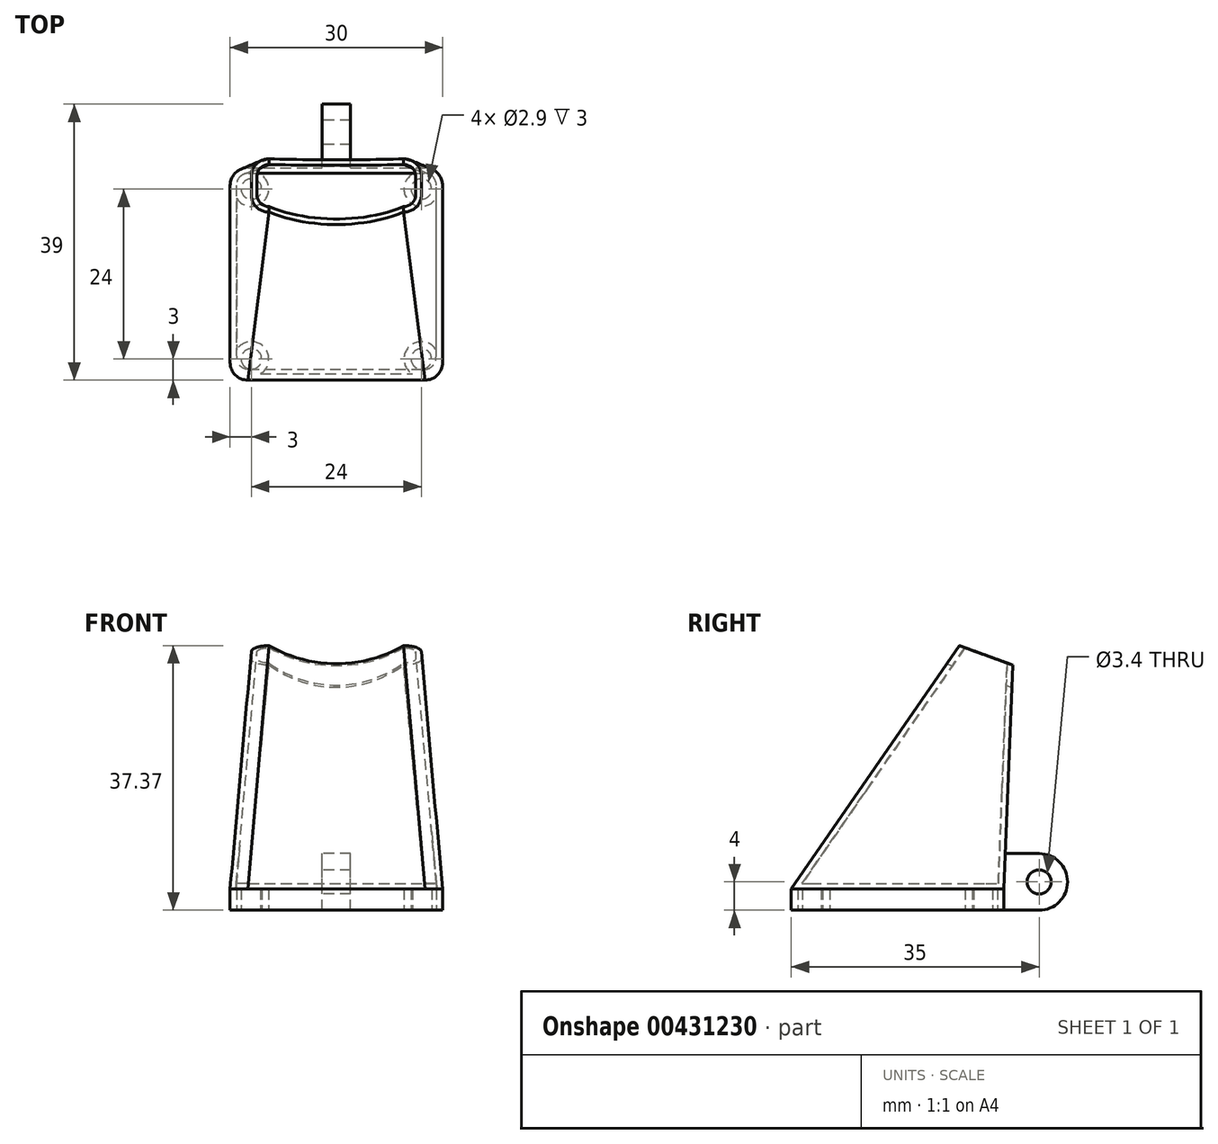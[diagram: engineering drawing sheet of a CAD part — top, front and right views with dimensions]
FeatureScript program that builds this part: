
annotation { "Feature Type Name" : "Feature", "Feature Type Description" : "" }
export const myFeature = defineFeature(function(context is Context, id is Id, definition is map)
    precondition{}
    {
        {
            var Q0;
            Q0=qCreatedBy(makeId("Top.planeOp"),FACE);
            var sketch = newSketch(context, id + "F0", { "sketchPlane" : qUnion([Q0])});
            skLineSegment(sketch, "E0", {"start": v(-15, 0) * mm, "end": v(-15, 12.5) * mm});
            skLineSegment(sketch, "E1", {"start": v(-12.5, 15) * mm, "end": v(0, 15) * mm});
            skPoint(sketch, "E2.visualSharp", {"position": v(-15, 15) * mm});
            skArc(sketch, "E2.filletArc", {"start": v(-12.5, 15) * mm, "mid": v(-14.27, 14.27) * mm, "end": v(-15, 12.5) * mm});
            skCircle(sketch, "E3", {"center": v(-12, 12) * mm, "radius": 1.45 * mm});
            skLineSegment(sketch, "E4", {"start": v(0, 14.1) * mm, "end": v(-10.74, 14.1) * mm});
            skLineSegment(sketch, "E5", {"start": v(-14.1, 0) * mm, "end": v(-14.1, 10.74) * mm});
            skArc(sketch, "E6", {"start": v(-10.74, 14.1) * mm, "mid": v(-10.27, 10.27) * mm, "end": v(-14.1, 10.74) * mm});
            skLineSegment(sketch, "E7.MirrorCS", {"start": v(12.5, 15) * mm, "end": v(0, 15) * mm});
            skArc(sketch, "E8.MirrorCS", {"start": v(12.5, 15) * mm, "mid": v(14.27, 14.27) * mm, "end": v(15, 12.5) * mm});
            skCircle(sketch, "E9.MirrorC", {"center": v(12, 12) * mm, "radius": 1.45 * mm});
            skPoint(sketch, "E10.MirrorP", {"position": v(15, 15) * mm});
            skLineSegment(sketch, "E11.MirrorCS", {"start": v(15, 0) * mm, "end": v(15, 12.5) * mm});
            skArc(sketch, "E12.MirrorCS", {"start": v(10.74, 14.1) * mm, "mid": v(10.27, 10.27) * mm, "end": v(14.1, 10.74) * mm});
            skLineSegment(sketch, "E13.MirrorCS", {"start": v(14.1, 0) * mm, "end": v(14.1, 10.74) * mm});
            skLineSegment(sketch, "E14.MirrorCS", {"start": v(0, 14.1) * mm, "end": v(10.74, 14.1) * mm});
            skLineSegment(sketch, "E15.MirrorCS", {"start": v(-14.1, 0) * mm, "end": v(-14.1, -10.74) * mm});
            skArc(sketch, "E16.MirrorCS", {"start": v(12.5, -15) * mm, "mid": v(14.27, -14.27) * mm, "end": v(15, -12.5) * mm});
            skLineSegment(sketch, "E17.MirrorCS", {"start": v(12.5, -15) * mm, "end": v(0, -15) * mm});
            skCircle(sketch, "E18.MirrorC", {"center": v(12, -12) * mm, "radius": 1.45 * mm});
            skLineSegment(sketch, "E19.MirrorCS", {"start": v(15, 0) * mm, "end": v(15, -12.5) * mm});
            skArc(sketch, "E20.MirrorCS", {"start": v(10.74, -14.1) * mm, "mid": v(10.27, -10.27) * mm, "end": v(14.1, -10.74) * mm});
            skLineSegment(sketch, "E21.MirrorCS", {"start": v(14.1, 0) * mm, "end": v(14.1, -10.74) * mm});
            skLineSegment(sketch, "E22.MirrorCS", {"start": v(-15, 0) * mm, "end": v(-15, -12.5) * mm});
            skLineSegment(sketch, "E23.MirrorCS", {"start": v(0, -14.1) * mm, "end": v(10.74, -14.1) * mm});
            skPoint(sketch, "E24.MirrorP", {"position": v(15, -15) * mm});
            skLineSegment(sketch, "E25.MirrorCS", {"start": v(0, -14.1) * mm, "end": v(-10.74, -14.1) * mm});
            skArc(sketch, "E26.MirrorCS", {"start": v(-10.74, -14.1) * mm, "mid": v(-10.27, -10.27) * mm, "end": v(-14.1, -10.74) * mm});
            skArc(sketch, "E27.MirrorCS", {"start": v(-12.5, -15) * mm, "mid": v(-14.27, -14.27) * mm, "end": v(-15, -12.5) * mm});
            skLineSegment(sketch, "E28.MirrorCS", {"start": v(-12.5, -15) * mm, "end": v(0, -15) * mm});
            skCircle(sketch, "E29.MirrorC", {"center": v(-12, -12) * mm, "radius": 1.45 * mm});
            skPoint(sketch, "E30.MirrorP", {"position": v(-15, -15) * mm});
            skSolve(sketch);
        }
        {
            var Q0;
            Q0 = qSketchRegion(id + "F0", true);
            extrude(context, id + "F1", {"entities" : qUnion([Q0]), "depth" : 3 * mm});
        }
        {
            var Q0;
            Q0=qCreatedBy(makeId("Right.planeOp"),FACE);
            var sketch = newSketch(context, id + "F2", { "sketchPlane" : qUnion([Q0])});
            skLineSegment(sketch, "E31.0", {"start": v(12.5, 3) * mm, "end": v(-12.5, 3) * mm, "construction": true});
            skLineSegment(sketch, "E32", {"start": v(0, 3) * mm, "end": v(0, 36) * mm, "construction": true});
            skPoint(sketch, "E32.endSnap0", {"position": v(0, 3) * mm});
            skLineSegment(sketch, "E33", {"start": v(12.5, 3) * mm, "end": v(12.5, 36) * mm, "construction": true});
            skLineSegment(sketch, "E34", {"start": v(6.18, 38.3) * mm, "end": v(18.52, 33.8) * mm, "construction": true});
            skSolve(sketch);
        }
        {
            var Q0;
            Q0=sQuery(id+"F2.wireOp",EDGE,"E34");
            cPlane(context, id + "F3", {"entities" : qUnion([Q0]), "cplaneType" : CPlaneType.LINE_ANGLE, "offset" : 25 * mm, "angle" : 0 * degree, "width" : 150 * mm, "height" : 150 * mm});
        }
        {
            var Q0;
            Q0=qCreatedBy(id+"F3.planeOp",FACE);
            var sketch = newSketch(context, id + "F4", { "sketchPlane" : qUnion([Q0])});
            skLineSegment(sketch, "E35", {"start": v(0, -0.57) * mm, "end": v(-15.7, -0.57) * mm});
            skLineSegment(sketch, "E36.0", {"start": v(-15, -12.77) * mm, "end": v(-15, 10.72) * mm, "construction": true});
            skLineSegment(sketch, "E37.0", {"start": v(15, 10.72) * mm, "end": v(15, -12.77) * mm, "construction": true});
            skLineSegment(sketch, "E38.bottom", {"start": v(-9.5, -4.57) * mm, "end": v(9.5, -4.57) * mm});
            skLineSegment(sketch, "E38.top", {"start": v(-9.5, 3.43) * mm, "end": v(9.5, 3.43) * mm});
            skLineSegment(sketch, "E38.left", {"start": v(-12, -2.07) * mm, "end": v(-12, 0.93) * mm});
            skLineSegment(sketch, "E38.right", {"start": v(12, -2.07) * mm, "end": v(12, 0.93) * mm});
            skPoint(sketch, "E39.visualSharp", {"position": v(-12, 3.43) * mm});
            skArc(sketch, "E39.filletArc", {"start": v(-9.5, 3.43) * mm, "mid": v(-11.27, 2.7) * mm, "end": v(-12, 0.93) * mm});
            skPoint(sketch, "E40.visualSharp", {"position": v(-12, -4.57) * mm});
            skArc(sketch, "E40.filletArc", {"start": v(-12, -2.07) * mm, "mid": v(-11.27, -3.83) * mm, "end": v(-9.5, -4.57) * mm});
            skPoint(sketch, "E41.visualSharp", {"position": v(12, -4.57) * mm});
            skArc(sketch, "E41.filletArc", {"start": v(9.5, -4.57) * mm, "mid": v(11.27, -3.83) * mm, "end": v(12, -2.07) * mm});
            skPoint(sketch, "E42.visualSharp", {"position": v(12, 3.43) * mm});
            skArc(sketch, "E42.filletArc", {"start": v(12, 0.93) * mm, "mid": v(11.27, 2.7) * mm, "end": v(9.5, 3.43) * mm});
            skSolve(sketch);
        }
        {
            var Q0;
            Q0=makeQuery(id+"F1.opExtrude","CAP_FACE",FACE,{"disambiguationData":[OSD([sQuery(id+"F0.wireOp",EDGE,"E0"),sQuery(id+"F0.wireOp",EDGE,"E1"),sQuery(id+"F0.wireOp",EDGE,"E2.filletArc"),sQuery(id+"F0.wireOp",EDGE,"E3"),sQuery(id+"F0.wireOp",EDGE,"E4"),sQuery(id+"F0.wireOp",EDGE,"E5"),sQuery(id+"F0.wireOp",EDGE,"E6"),sQuery(id+"F0.wireOp",EDGE,"E7.MirrorCS"),sQuery(id+"F0.wireOp",EDGE,"E8.MirrorCS"),sQuery(id+"F0.wireOp",EDGE,"E9.MirrorC"),sQuery(id+"F0.wireOp",EDGE,"E11.MirrorCS"),sQuery(id+"F0.wireOp",EDGE,"E12.MirrorCS"),sQuery(id+"F0.wireOp",EDGE,"E13.MirrorCS"),sQuery(id+"F0.wireOp",EDGE,"E14.MirrorCS"),sQuery(id+"F0.wireOp",EDGE,"E15.MirrorCS"),sQuery(id+"F0.wireOp",EDGE,"E16.MirrorCS"),sQuery(id+"F0.wireOp",EDGE,"E17.MirrorCS"),sQuery(id+"F0.wireOp",EDGE,"E18.MirrorC"),sQuery(id+"F0.wireOp",EDGE,"E19.MirrorCS"),sQuery(id+"F0.wireOp",EDGE,"E20.MirrorCS"),sQuery(id+"F0.wireOp",EDGE,"E21.MirrorCS"),sQuery(id+"F0.wireOp",EDGE,"E22.MirrorCS"),sQuery(id+"F0.wireOp",EDGE,"E23.MirrorCS"),sQuery(id+"F0.wireOp",EDGE,"E25.MirrorCS"),sQuery(id+"F0.wireOp",EDGE,"E26.MirrorCS"),sQuery(id+"F0.wireOp",EDGE,"E27.MirrorCS"),sQuery(id+"F0.wireOp",EDGE,"E28.MirrorCS"),sQuery(id+"F0.wireOp",EDGE,"E29.MirrorC")])],"isStart":false});
            var sketch = newSketch(context, id + "F5", { "sketchPlane" : qUnion([Q0])});
            skArc(sketch, "E43.0", {"start": v(-12.5, -15) * mm, "mid": v(-14.27, -14.27) * mm, "end": v(-15, -12.5) * mm});
            skLineSegment(sketch, "E44.0", {"start": v(-15, -12.5) * mm, "end": v(-15, 12.5) * mm});
            skArc(sketch, "E45.0", {"start": v(-12.5, 15) * mm, "mid": v(-14.27, 14.27) * mm, "end": v(-15, 12.5) * mm});
            skLineSegment(sketch, "E46.0", {"start": v(12.5, 15) * mm, "end": v(-12.5, 15) * mm});
            skArc(sketch, "E47.0", {"start": v(12.5, 15) * mm, "mid": v(14.27, 14.27) * mm, "end": v(15, 12.5) * mm});
            skLineSegment(sketch, "E48.0", {"start": v(15, 12.5) * mm, "end": v(15, -12.5) * mm});
            skArc(sketch, "E49.0", {"start": v(12.5, -15) * mm, "mid": v(14.27, -14.27) * mm, "end": v(15, -12.5) * mm});
            skLineSegment(sketch, "E50.0", {"start": v(12.5, -15) * mm, "end": v(-12.5, -15) * mm});
            skSolve(sketch);
        }
        {
            var Q1;
            Q1 = qSketchRegion(id + "F5", true);
            var Q2;
            Q2=makeQuery(id+"F4.imprint","IMPRINT",FACE,{"disambiguationData":[TD([[makeQuery(id+"F4.imprint","IMPRINT",EDGE,{"derivedFrom":sQuery(id+"F4.wireOp",EDGE,"E38.bottom")}),1.0]])]});
            loft(context, id + "F6", {"sheetProfilesArray" : [{ "sheetProfileEntities" : qUnion([Q1]) }, { "sheetProfileEntities" : qUnion([Q2]) }]});
        }
        {
            var Q0;
            Q0=makeQuery(id+"F6.opLoft","CAP_FACE",FACE,{"disambiguationData":[OSD([makeQuery(id+"F5.imprint","IMPRINT",FACE,{"disambiguationData":[TD([[makeQuery(id+"F5.imprint","IMPRINT",EDGE,{"derivedFrom":sQuery(id+"F5.wireOp",EDGE,"E43.0")}),-1.0]])]})])],"isStart":true});
            var Q1;
            Q1=makeQuery(id+"F6.opLoft","CAP_FACE",FACE,{"disambiguationData":[OSD([makeQuery(id+"F4.imprint","IMPRINT",FACE,{"disambiguationData":[TD([[makeQuery(id+"F4.imprint","IMPRINT",EDGE,{"derivedFrom":sQuery(id+"F4.wireOp",EDGE,"E38.bottom")}),1.0]])]})])],"isStart":true});
            shell(context, id + "F7", {"entities" : qUnion([Q0, Q1]), "thickness" : 0.8 * mm});
        }
        {
            var Q0;
            Q0=makeQuery(id+"F6.opLoft","SWEPT_BODY",BODY,{"disambiguationData":[OSD([makeQuery(id+"F4.imprint","IMPRINT",FACE,{"disambiguationData":[TD([[makeQuery(id+"F4.imprint","IMPRINT",EDGE,{"derivedFrom":sQuery(id+"F4.wireOp",EDGE,"E38.bottom")}),1.0]])]}),makeQuery(id+"F5.imprint","IMPRINT",FACE,{"disambiguationData":[TD([[makeQuery(id+"F5.imprint","IMPRINT",EDGE,{"derivedFrom":makeQuery(id+"F1.opExtrude","CAP_EDGE",EDGE,{"disambiguationData":[OSD([sQuery(id+"F0.wireOp",EDGE,"E3")])],"isStart":false})}),1.0]])]})])]});
            var Q1;
            Q1=makeQuery(id+"F1.opExtrude","SWEPT_BODY",BODY,{"disambiguationData":[OSD([sQuery(id+"F0.wireOp",EDGE,"E0"),sQuery(id+"F0.wireOp",EDGE,"E1"),sQuery(id+"F0.wireOp",EDGE,"E2.filletArc"),sQuery(id+"F0.wireOp",EDGE,"E3"),sQuery(id+"F0.wireOp",EDGE,"E4"),sQuery(id+"F0.wireOp",EDGE,"E5"),sQuery(id+"F0.wireOp",EDGE,"E6"),sQuery(id+"F0.wireOp",EDGE,"E7.MirrorCS"),sQuery(id+"F0.wireOp",EDGE,"E8.MirrorCS"),sQuery(id+"F0.wireOp",EDGE,"E9.MirrorC"),sQuery(id+"F0.wireOp",EDGE,"E11.MirrorCS"),sQuery(id+"F0.wireOp",EDGE,"E12.MirrorCS"),sQuery(id+"F0.wireOp",EDGE,"E13.MirrorCS"),sQuery(id+"F0.wireOp",EDGE,"E14.MirrorCS"),sQuery(id+"F0.wireOp",EDGE,"E15.MirrorCS"),sQuery(id+"F0.wireOp",EDGE,"E16.MirrorCS"),sQuery(id+"F0.wireOp",EDGE,"E17.MirrorCS"),sQuery(id+"F0.wireOp",EDGE,"E18.MirrorC"),sQuery(id+"F0.wireOp",EDGE,"E19.MirrorCS"),sQuery(id+"F0.wireOp",EDGE,"E20.MirrorCS"),sQuery(id+"F0.wireOp",EDGE,"E21.MirrorCS"),sQuery(id+"F0.wireOp",EDGE,"E22.MirrorCS"),sQuery(id+"F0.wireOp",EDGE,"E23.MirrorCS"),sQuery(id+"F0.wireOp",EDGE,"E25.MirrorCS"),sQuery(id+"F0.wireOp",EDGE,"E26.MirrorCS"),sQuery(id+"F0.wireOp",EDGE,"E27.MirrorCS"),sQuery(id+"F0.wireOp",EDGE,"E28.MirrorCS"),sQuery(id+"F0.wireOp",EDGE,"E29.MirrorC")])]});
            booleanBodies(context, id + "F8", {"operationType" : BooleanOperationType.UNION, "tools" : qUnion([Q0, Q1])});
        }
        {
            var Q0;
            Q0=qCreatedBy(makeId("Right.planeOp"),FACE);
            var sketch = newSketch(context, id + "F9", { "sketchPlane" : qUnion([Q0])});
            skLineSegment(sketch, "E51.0", {"start": v(15, 3) * mm, "end": v(15, 0) * mm, "construction": true});
            skLineSegment(sketch, "E52.bottom", {"start": v(15, 0) * mm, "end": v(24, 0) * mm});
            skLineSegment(sketch, "E52.top", {"start": v(15, 8) * mm, "end": v(24, 8) * mm});
            skLineSegment(sketch, "E52.left", {"start": v(15, 0) * mm, "end": v(15, 8) * mm});
            skLineSegment(sketch, "E52.right", {"start": v(24, 0) * mm, "end": v(24, 8) * mm});
            skLineSegment(sketch, "E53", {"start": v(23.3, 4) * mm, "end": v(17.02, 4) * mm, "construction": true});
            skPoint(sketch, "E53.startSnap0", {"position": v(24, 4) * mm});
            skCircle(sketch, "E54", {"center": v(20, 4) * mm, "radius": 1.7 * mm});
            skSolve(sketch);
        }
        {
            var Q0;
            Q0 = qSketchRegion(id + "F9", true);
            extrude(context, id + "F10", {"entities" : qUnion([Q0]), "operationType" : NewBodyOperationType.ADD, "depth" : 4 * mm, "symmetric" : true});
        }
        {
            var Q0;
            Q0=makeQuery(id+"F10.opExtrude","SWEPT_EDGE",EDGE,{"disambiguationData":[OSD([sQuery(id+"F9.wireOp",EDGE,"E52.top"),sQuery(id+"F9.wireOp",EDGE,"E52.right")])]});
            var Q1;
            Q1=makeQuery(id+"F10.opExtrude","SWEPT_EDGE",EDGE,{"disambiguationData":[OSD([sQuery(id+"F9.wireOp",EDGE,"E52.bottom"),sQuery(id+"F9.wireOp",EDGE,"E52.right")])]});
            fillet(context, id + "F11", {"entities" : qUnion([Q0, Q1]), "radius" : 4 * mm, "tangentPropagation" : true, "allowEdgeOverflow" : false});
        }
        {
            var Q0;
            Q0=sQuery(id+"F2.wireOp",VERTEX,"E33.end");
            var Q1;
            Q1=sQuery(id+"F2.wireOp",EDGE,"E34");
            cPlane(context, id + "F12", {"entities" : qUnion([Q0, Q1]), "cplaneType" : CPlaneType.LINE_POINT, "offset" : 25 * mm, "width" : 150 * mm, "height" : 150 * mm});
        }
        {
            var Q0;
            Q0=qCreatedBy(id+"F12.planeOp",FACE);
            var sketch = newSketch(context, id + "F13", { "sketchPlane" : qUnion([Q0])});
            skLineSegment(sketch, "E55.0.0", {"start": v(-2, 7.95) * mm, "end": v(-2, 12.72) * mm, "construction": true});
            skLineSegment(sketch, "E55.0.1", {"start": v(-2, 12.72) * mm, "end": v(2, 12.72) * mm, "construction": true});
            skLineSegment(sketch, "E55.0.2", {"start": v(2, 12.72) * mm, "end": v(2, 7.95) * mm, "construction": true});
            skLineSegment(sketch, "E55.0.3", {"start": v(2, 7.95) * mm, "end": v(12.5, 7.95) * mm, "construction": true});
            skFitSpline(sketch, "E55.0.4", {"points": [v(12.5, 7.95) * mm, v(11.5, 18) * mm, v(10.5, 28.05) * mm, v(9.5, 38.1) * mm], "construction": true});
            skLineSegment(sketch, "E55.0.5", {"start": v(-9.5, 38.1) * mm, "end": v(9.5, 38.1) * mm, "construction": true});
            skFitSpline(sketch, "E55.0.6", {"points": [v(-9.5, 38.1) * mm, v(-10.5, 28.05) * mm, v(-11.5, 18) * mm, v(-12.5, 7.95) * mm], "construction": true});
            skLineSegment(sketch, "E55.0.7", {"start": v(-12.5, 7.95) * mm, "end": v(-2, 7.95) * mm, "construction": true});
            skPoint(sketch, "E56.0", {"position": v(0, 33.83) * mm});
            skArc(sketch, "E57", {"start": v(-9.5, 38.1) * mm, "mid": v(0, 35.1) * mm, "end": v(9.5, 38.1) * mm});
            skLineSegment(sketch, "E58.0", {"start": v(-9.5, 38.1) * mm, "end": v(9.5, 38.1) * mm});
            skSolve(sketch);
        }
        {
            var Q0;
            Q0 = qSketchRegion(id + "F13", true);
            var Q1;
            Q1=makeQuery(id+"F6.opLoft","SWEPT_BODY",BODY,{"disambiguationData":[OSD([makeQuery(id+"F4.imprint","IMPRINT",FACE,{"disambiguationData":[TD([[makeQuery(id+"F4.imprint","IMPRINT",EDGE,{"derivedFrom":sQuery(id+"F4.wireOp",EDGE,"E38.bottom")}),1.0]])]}),makeQuery(id+"F5.imprint","IMPRINT",FACE,{"disambiguationData":[TD([[makeQuery(id+"F5.imprint","IMPRINT",EDGE,{"derivedFrom":makeQuery(id+"F1.opExtrude","CAP_EDGE",EDGE,{"disambiguationData":[OSD([sQuery(id+"F0.wireOp",EDGE,"E3")])],"isStart":false})}),1.0]])]})])]});
            extrude(context, id + "F14", {"entities" : qUnion([Q0]), "operationType" : NewBodyOperationType.REMOVE, "oppositeDirection" : true, "depth" : 25 * mm, "symmetric" : true});
        }
    });
